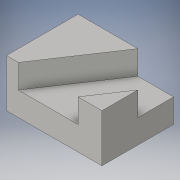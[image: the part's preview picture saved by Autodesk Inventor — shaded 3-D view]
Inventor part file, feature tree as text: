
AUTODESK INVENTOR PART (.ipt)
format: ipt  version: 2016 (Build 200138000, 138)  size: 104,960 bytes
history: native  units: in
note: dims shown in document units (in); Inventor stores cm internally (conversion verified against a paired STEP export)
features: extrude x2, sketch x2
ambient origin geometry x8: Origin, YZ Plane, XZ Plane, XY Plane, X Axis, Y Axis, Z Axis, Center Point
bodies: Solid1 (feature_tree)
feature tree (4):
  extrude  "Extrusion1"  Depth=1.0in
  extrude  "Extrusion3"  Depth=0.5in
  sketch  "Sketch1"  dims[d0=2.0in d1=1.0in]
  sketch  "Sketch4"  dims[d2=1.5in d3=0.0in d10=0.25in d11=0.5in d12=0.75in d13=1.25in d14=0.5in d15=0.0in]
